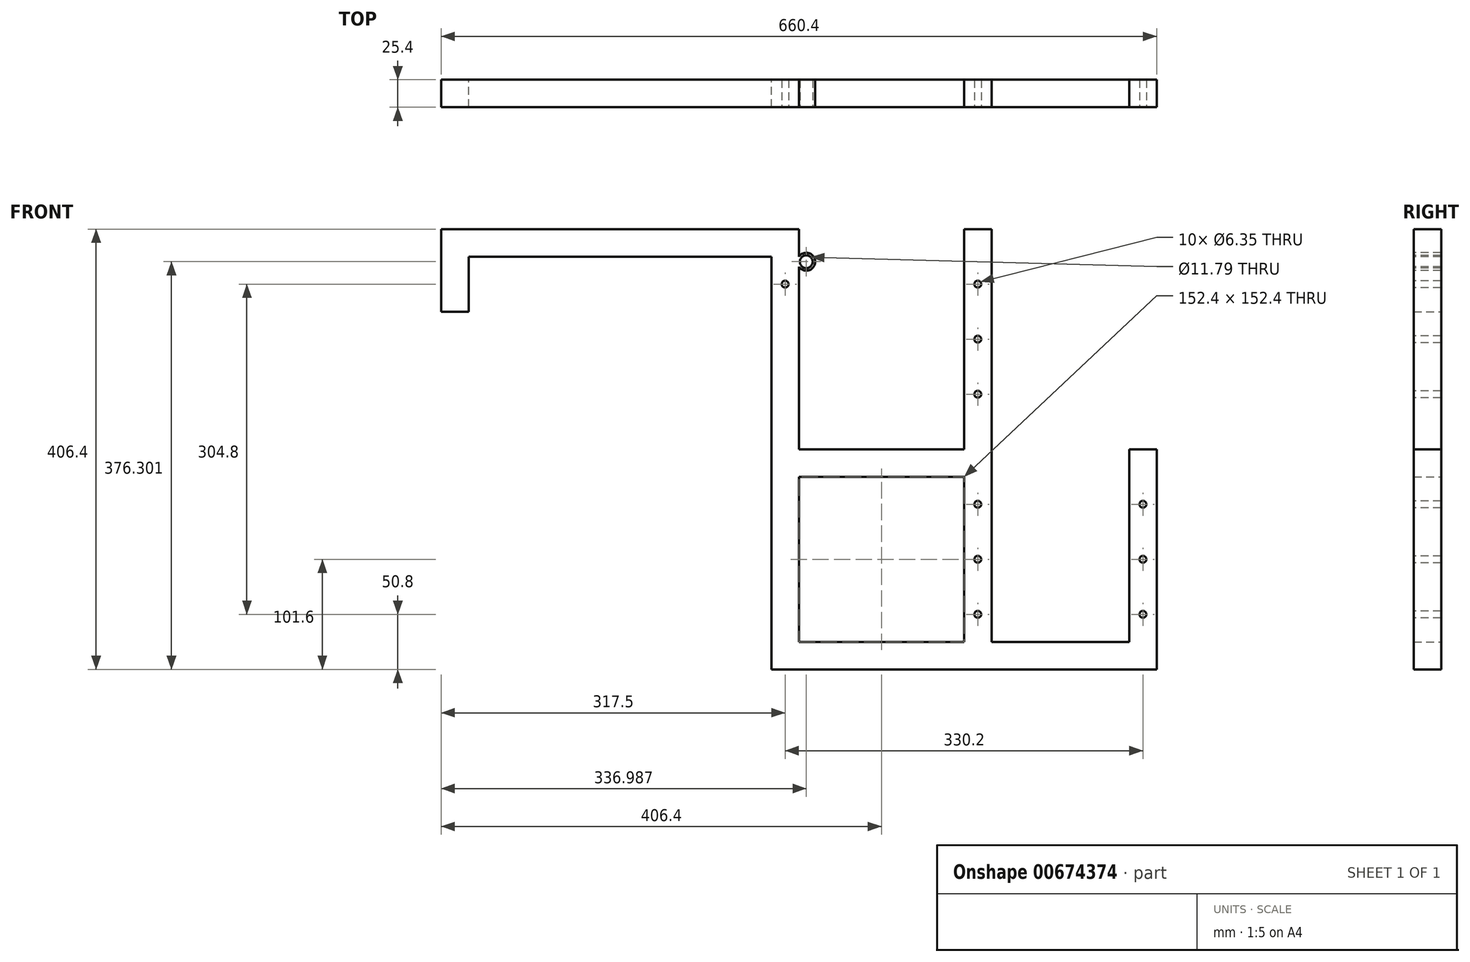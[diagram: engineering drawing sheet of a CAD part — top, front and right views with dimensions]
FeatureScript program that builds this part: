
annotation { "Feature Type Name" : "Feature", "Feature Type Description" : "" }
export const myFeature = defineFeature(function(context is Context, id is Id, definition is map)
    precondition{}
    {
        {
            var Q0;
            Q0=qCreatedBy(makeId("Front.planeOp"),FACE);
            var sketch = newSketch(context, id + "F0", { "sketchPlane" : qUnion([Q0])});
            skLineSegment(sketch, "E0.bottom", {"start": v(0, 0) * mm, "end": v(279.4, 0) * mm});
            skLineSegment(sketch, "E0.top", {"start": v(0, -25.4) * mm, "end": v(279.4, -25.4) * mm});
            skLineSegment(sketch, "E0.left", {"start": v(0, 0) * mm, "end": v(0, -25.4) * mm});
            skLineSegment(sketch, "E0.right", {"start": v(279.4, 0) * mm, "end": v(279.4, -25.4) * mm});
            skLineSegment(sketch, "E1.bottom", {"start": v(0, 0) * mm, "end": v(-25.4, 0) * mm});
            skLineSegment(sketch, "E1.top", {"start": v(0, -76.2) * mm, "end": v(-25.4, -76.2) * mm});
            skLineSegment(sketch, "E1.left", {"start": v(0, 0) * mm, "end": v(0, -76.2) * mm});
            skLineSegment(sketch, "E1.right", {"start": v(-25.4, 0) * mm, "end": v(-25.4, -76.2) * mm});
            skLineSegment(sketch, "E2.bottom", {"start": v(279.4, 0) * mm, "end": v(304.8, 0) * mm});
            skLineSegment(sketch, "E2.top", {"start": v(279.4, -406.4) * mm, "end": v(304.8, -406.4) * mm});
            skLineSegment(sketch, "E2.left", {"start": v(279.4, 0) * mm, "end": v(279.4, -406.4) * mm});
            skLineSegment(sketch, "E2.right", {"start": v(304.8, 0) * mm, "end": v(304.8, -406.4) * mm});
            skLineSegment(sketch, "E3.bottom", {"start": v(304.8, -203.2) * mm, "end": v(457.2, -203.2) * mm});
            skLineSegment(sketch, "E3.top", {"start": v(304.8, -228.6) * mm, "end": v(457.2, -228.6) * mm});
            skLineSegment(sketch, "E3.left", {"start": v(304.8, -203.2) * mm, "end": v(304.8, -228.6) * mm});
            skLineSegment(sketch, "E3.right", {"start": v(457.2, -203.2) * mm, "end": v(457.2, -228.6) * mm});
            skLineSegment(sketch, "E4.bottom", {"start": v(304.8, -406.4) * mm, "end": v(609.6, -406.4) * mm});
            skLineSegment(sketch, "E4.top", {"start": v(304.8, -381) * mm, "end": v(609.6, -381) * mm});
            skLineSegment(sketch, "E4.left", {"start": v(304.8, -406.4) * mm, "end": v(304.8, -381) * mm});
            skLineSegment(sketch, "E4.right", {"start": v(609.6, -406.4) * mm, "end": v(609.6, -381) * mm});
            skLineSegment(sketch, "E5.bottom", {"start": v(457.2, -406.4) * mm, "end": v(482.6, -406.4) * mm});
            skLineSegment(sketch, "E5.top", {"start": v(457.2, 0) * mm, "end": v(482.6, 0) * mm});
            skLineSegment(sketch, "E5.left", {"start": v(457.2, -406.4) * mm, "end": v(457.2, 0) * mm});
            skLineSegment(sketch, "E5.right", {"start": v(482.6, -406.4) * mm, "end": v(482.6, 0) * mm});
            skPoint(sketch, "E6.oppositeSnap0", {"position": v(482.6, -203.2) * mm});
            skLineSegment(sketch, "E6.bottom", {"start": v(609.6, -406.4) * mm, "end": v(635, -406.4) * mm});
            skLineSegment(sketch, "E6.top", {"start": v(609.6, -203.2) * mm, "end": v(635, -203.2) * mm});
            skLineSegment(sketch, "E6.left", {"start": v(609.6, -406.4) * mm, "end": v(609.6, -203.2) * mm});
            skLineSegment(sketch, "E6.right", {"start": v(635, -406.4) * mm, "end": v(635, -203.2) * mm});
            skSolve(sketch);
        }
        {
            var Q0;
            Q0 = qSketchRegion(id + "F0", true);
            extrude(context, id + "F1", {"entities" : qUnion([Q0]), "endBound" : BoundingType.SYMMETRIC, "depth" : 25.4 * mm, "offsetDistance" : 25.4 * mm});
        }
        {
            var Q0;
            Q0=makeQuery(id+"F1.opExtrude","CAP_FACE",FACE,{"disambiguationData":[OSD([sQuery(id+"F0.wireOp",EDGE,"E0.bottom"),sQuery(id+"F0.wireOp",EDGE,"E0.top"),sQuery(id+"F0.wireOp",EDGE,"E1.bottom"),sQuery(id+"F0.wireOp",EDGE,"E1.top"),sQuery(id+"F0.wireOp",EDGE,"E1.left"),sQuery(id+"F0.wireOp",EDGE,"E1.right"),sQuery(id+"F0.wireOp",EDGE,"E2.bottom"),sQuery(id+"F0.wireOp",EDGE,"E2.top"),sQuery(id+"F0.wireOp",EDGE,"E2.left"),sQuery(id+"F0.wireOp",EDGE,"E2.right"),sQuery(id+"F0.wireOp",EDGE,"E3.bottom"),sQuery(id+"F0.wireOp",EDGE,"E3.top"),sQuery(id+"F0.wireOp",EDGE,"E4.bottom"),sQuery(id+"F0.wireOp",EDGE,"E4.top"),sQuery(id+"F0.wireOp",EDGE,"E5.bottom"),sQuery(id+"F0.wireOp",EDGE,"E5.top"),sQuery(id+"F0.wireOp",EDGE,"E5.left"),sQuery(id+"F0.wireOp",EDGE,"E5.right"),sQuery(id+"F0.wireOp",EDGE,"E6.bottom"),sQuery(id+"F0.wireOp",EDGE,"E6.top"),sQuery(id+"F0.wireOp",EDGE,"E6.left"),sQuery(id+"F0.wireOp",EDGE,"E6.right")])],"isStart":false});
            var sketch = newSketch(context, id + "F2", { "sketchPlane" : qUnion([Q0])});
            skCircle(sketch, "E7", {"center": v(469.9, -101.6) * mm, "radius": 3.18 * mm});
            skCircle(sketch, "E8", {"center": v(469.9, -50.8) * mm, "radius": 3.18 * mm});
            skCircle(sketch, "E9", {"center": v(469.9, -152.4) * mm, "radius": 3.18 * mm});
            skCircle(sketch, "E10", {"center": v(469.9, -304.8) * mm, "radius": 3.17 * mm});
            skCircle(sketch, "E11", {"center": v(469.9, -254) * mm, "radius": 3.17 * mm});
            skCircle(sketch, "E12", {"center": v(469.9, -355.6) * mm, "radius": 3.17 * mm});
            skCircle(sketch, "E13", {"center": v(622.3, -304.8) * mm, "radius": 3.18 * mm});
            skCircle(sketch, "E14", {"center": v(622.3, -254) * mm, "radius": 3.18 * mm});
            skCircle(sketch, "E15", {"center": v(622.3, -355.6) * mm, "radius": 3.17 * mm});
            skCircle(sketch, "E16", {"center": v(292.1, -50.8) * mm, "radius": 3.17 * mm});
            skSolve(sketch);
        }
        {
            var Q0;
            Q0 = qSketchRegion(id + "F2", true);
            extrude(context, id + "F3", {"entities" : qUnion([Q0]), "operationType" : NewBodyOperationType.REMOVE, "depth" : 50.8 * mm, "offsetDistance" : 25.4 * mm});
        }
        {
            var Q0;
            Q0 = qSketchRegion(id + "F2", true);
            extrude(context, id + "F4", {"entities" : qUnion([Q0]), "operationType" : NewBodyOperationType.REMOVE, "oppositeDirection" : true, "depth" : 25.4 * mm, "offsetDistance" : 25.4 * mm});
        }
        {
            var Q0;
            Q0=makeQuery(id+"F1.opExtrude","CAP_FACE",FACE,{"disambiguationData":[OSD([sQuery(id+"F0.wireOp",EDGE,"E0.bottom"),sQuery(id+"F0.wireOp",EDGE,"E0.top"),sQuery(id+"F0.wireOp",EDGE,"E1.bottom"),sQuery(id+"F0.wireOp",EDGE,"E1.top"),sQuery(id+"F0.wireOp",EDGE,"E1.left"),sQuery(id+"F0.wireOp",EDGE,"E1.right"),sQuery(id+"F0.wireOp",EDGE,"E2.bottom"),sQuery(id+"F0.wireOp",EDGE,"E2.top"),sQuery(id+"F0.wireOp",EDGE,"E2.left"),sQuery(id+"F0.wireOp",EDGE,"E2.right"),sQuery(id+"F0.wireOp",EDGE,"E3.bottom"),sQuery(id+"F0.wireOp",EDGE,"E3.top"),sQuery(id+"F0.wireOp",EDGE,"E4.bottom"),sQuery(id+"F0.wireOp",EDGE,"E4.top"),sQuery(id+"F0.wireOp",EDGE,"E5.bottom"),sQuery(id+"F0.wireOp",EDGE,"E5.top"),sQuery(id+"F0.wireOp",EDGE,"E5.left"),sQuery(id+"F0.wireOp",EDGE,"E5.right"),sQuery(id+"F0.wireOp",EDGE,"E6.bottom"),sQuery(id+"F0.wireOp",EDGE,"E6.top"),sQuery(id+"F0.wireOp",EDGE,"E6.left"),sQuery(id+"F0.wireOp",EDGE,"E6.right")])],"isStart":false});
            var sketch = newSketch(context, id + "F5", { "sketchPlane" : qUnion([Q0])});
            skCircle(sketch, "E17", {"center": v(311.59, -30.1) * mm, "radius": 8.26 * mm});
            skPoint(sketch, "E17.first.point", {"position": v(304.8, -25.4) * mm});
            skPoint(sketch, "E17.second.point", {"position": v(319.39, -32.8) * mm});
            skPoint(sketch, "E17.third.point", {"position": v(313.44, -22.05) * mm});
            skSolve(sketch);
        }
        {
            var Q0;
            Q0 = qSketchRegion(id + "F5", true);
            extrude(context, id + "F6", {"entities" : qUnion([Q0]), "operationType" : NewBodyOperationType.ADD, "oppositeDirection" : true, "depth" : 25.4 * mm, "offsetDistance" : 25.4 * mm});
        }
        {
            var Q0;
            Q0=makeQuery(id+"F6.boolean.opBoolean","MERGE",FACE,{"derivedFrom":[makeQuery(id+"F1.opExtrude","CAP_FACE",FACE,{"disambiguationData":[OSD([sQuery(id+"F0.wireOp",EDGE,"E0.bottom"),sQuery(id+"F0.wireOp",EDGE,"E0.top"),sQuery(id+"F0.wireOp",EDGE,"E1.bottom"),sQuery(id+"F0.wireOp",EDGE,"E1.top"),sQuery(id+"F0.wireOp",EDGE,"E1.left"),sQuery(id+"F0.wireOp",EDGE,"E1.right"),sQuery(id+"F0.wireOp",EDGE,"E2.bottom"),sQuery(id+"F0.wireOp",EDGE,"E2.top"),sQuery(id+"F0.wireOp",EDGE,"E2.left"),sQuery(id+"F0.wireOp",EDGE,"E2.right"),sQuery(id+"F0.wireOp",EDGE,"E3.bottom"),sQuery(id+"F0.wireOp",EDGE,"E3.top"),sQuery(id+"F0.wireOp",EDGE,"E4.bottom"),sQuery(id+"F0.wireOp",EDGE,"E4.top"),sQuery(id+"F0.wireOp",EDGE,"E5.bottom"),sQuery(id+"F0.wireOp",EDGE,"E5.top"),sQuery(id+"F0.wireOp",EDGE,"E5.left"),sQuery(id+"F0.wireOp",EDGE,"E5.right"),sQuery(id+"F0.wireOp",EDGE,"E6.bottom"),sQuery(id+"F0.wireOp",EDGE,"E6.top"),sQuery(id+"F0.wireOp",EDGE,"E6.left"),sQuery(id+"F0.wireOp",EDGE,"E6.right")])],"isStart":false}),makeQuery(id+"F6.opExtrude","CAP_FACE",FACE,{"disambiguationData":[OSD([sQuery(id+"F5.wireOp",EDGE,"E17")])],"isStart":true})]});
            var sketch = newSketch(context, id + "F7", { "sketchPlane" : qUnion([Q0])});
            skArc(sketch, "E18", {"start": v(301.62, -123.82) * mm, "mid": v(381, -203.2) * mm, "end": v(460.38, -123.83) * mm});
            skPoint(sketch, "E18.first.point", {"position": v(381, -203.2) * mm});
            skPoint(sketch, "E18.second.point", {"position": v(304.8, -101.6) * mm});
            skPoint(sketch, "E18.third.point", {"position": v(457.2, -101.6) * mm});
            skArc(sketch, "E19", {"start": v(307.3, -123.82) * mm, "mid": v(381, -197.52) * mm, "end": v(454.7, -123.83) * mm});
            skLineSegment(sketch, "E20", {"start": v(301.62, -123.82) * mm, "end": v(307.3, -123.82) * mm});
            skLineSegment(sketch, "E21.trimOffspring", {"start": v(454.7, -123.82) * mm, "end": v(460.38, -123.82) * mm});
            skSolve(sketch);
        }
        {
            var Q0;
            Q0=sQuery(id+"F7.wireOp",EDGE,"E19");
            var Q1;
            Q1=sQuery(id+"F7.wireOp",EDGE,"E18");
            var Q2;
            Q2=sQuery(id+"F7.wireOp",EDGE,"E20");
            var Q3;
            Q3=sQuery(id+"F7.wireOp",EDGE,"E21.trimOffspring");
            extrude(context, id + "F8", {"bodyType" : ToolBodyType.SURFACE, "surfaceEntities" : qUnion([Q0, Q1, Q2, Q3]), "oppositeDirection" : true, "depth" : 762 * mm, "offsetDistance" : 25.4 * mm});
        }
        {
            var Q0;
            Q0=makeQuery(id+"F6.boolean.opBoolean","MERGE",FACE,{"derivedFrom":[makeQuery(id+"F1.opExtrude","CAP_FACE",FACE,{"disambiguationData":[OSD([sQuery(id+"F0.wireOp",EDGE,"E0.bottom"),sQuery(id+"F0.wireOp",EDGE,"E0.top"),sQuery(id+"F0.wireOp",EDGE,"E1.bottom"),sQuery(id+"F0.wireOp",EDGE,"E1.top"),sQuery(id+"F0.wireOp",EDGE,"E1.left"),sQuery(id+"F0.wireOp",EDGE,"E1.right"),sQuery(id+"F0.wireOp",EDGE,"E2.bottom"),sQuery(id+"F0.wireOp",EDGE,"E2.top"),sQuery(id+"F0.wireOp",EDGE,"E2.left"),sQuery(id+"F0.wireOp",EDGE,"E2.right"),sQuery(id+"F0.wireOp",EDGE,"E3.bottom"),sQuery(id+"F0.wireOp",EDGE,"E3.top"),sQuery(id+"F0.wireOp",EDGE,"E4.bottom"),sQuery(id+"F0.wireOp",EDGE,"E4.top"),sQuery(id+"F0.wireOp",EDGE,"E5.bottom"),sQuery(id+"F0.wireOp",EDGE,"E5.top"),sQuery(id+"F0.wireOp",EDGE,"E5.left"),sQuery(id+"F0.wireOp",EDGE,"E5.right"),sQuery(id+"F0.wireOp",EDGE,"E6.bottom"),sQuery(id+"F0.wireOp",EDGE,"E6.top"),sQuery(id+"F0.wireOp",EDGE,"E6.left"),sQuery(id+"F0.wireOp",EDGE,"E6.right")])],"isStart":false}),makeQuery(id+"F6.opExtrude","CAP_FACE",FACE,{"disambiguationData":[OSD([sQuery(id+"F5.wireOp",EDGE,"E17")])],"isStart":true})]});
            var sketch = newSketch(context, id + "F9", { "sketchPlane" : qUnion([Q0])});
            skCircle(sketch, "E22", {"center": v(311.59, -30.1) * mm, "radius": 5.9 * mm});
            skSolve(sketch);
        }
        {
            var Q0;
            Q0 = qSketchRegion(id + "F9", true);
            extrude(context, id + "F10", {"entities" : qUnion([Q0]), "operationType" : NewBodyOperationType.REMOVE, "oppositeDirection" : true, "depth" : 25.4 * mm, "offsetDistance" : 25.4 * mm});
        }
    });
